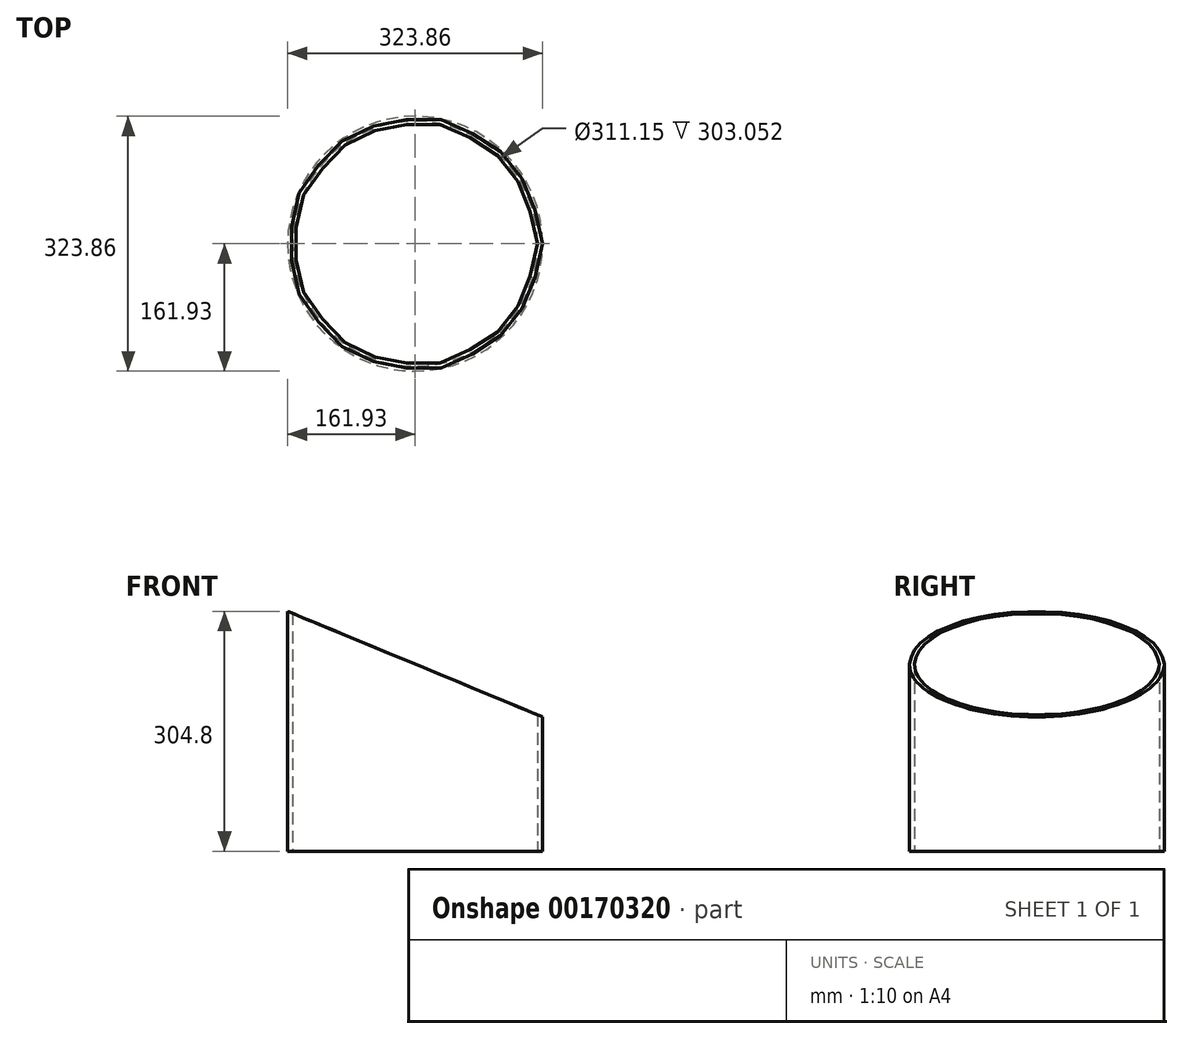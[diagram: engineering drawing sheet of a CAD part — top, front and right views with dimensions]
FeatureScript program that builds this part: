
annotation { "Feature Type Name" : "Feature", "Feature Type Description" : "" }
export const myFeature = defineFeature(function(context is Context, id is Id, definition is map)
    precondition{}
    {
        {
            var Q0;
            Q0=qCreatedBy(makeId("Top.planeOp"),FACE);
            var sketch = newSketch(context, id + "F0", { "sketchPlane" : qUnion([Q0])});
            skCircle(sketch, "E0", {"center": v(0, 0) * mm, "radius": 161.93 * mm});
            skCircle(sketch, "E1.0", {"center": v(0, 0) * mm, "radius": 155.58 * mm});
            skSolve(sketch);
        }
        {
            var Q0;
            Q0=makeQuery(id+"F0.imprint","IMPRINT",FACE,{"disambiguationData":[TD([[makeQuery(id+"F0.imprint","IMPRINT",EDGE,{"derivedFrom":sQuery(id+"F0.wireOp",EDGE,"E1.0")}),-1.0]])]});
            extrude(context, id + "F1", {"entities" : qUnion([Q0]), "depth" : 304.8 * mm});
        }
        {
            var Q0;
            Q0=qCreatedBy(makeId("Front.planeOp"),FACE);
            var sketch = newSketch(context, id + "F2", { "sketchPlane" : qUnion([Q0])});
            skLineSegment(sketch, "E2", {"start": v(0, 0) * mm, "end": v(0, 229.3) * mm, "construction": true});
            skLineSegment(sketch, "E3", {"start": v(0, 229.3) * mm, "end": v(-161.93, 229.3) * mm, "construction": true});
            skLineSegment(sketch, "E4", {"start": v(-161.93, 229.3) * mm, "end": v(-161.93, 304.8) * mm, "construction": true});
            skLineSegment(sketch, "E5", {"start": v(-161.93, 304.8) * mm, "end": v(161.93, 170.66) * mm});
            skLineSegment(sketch, "E6", {"start": v(-161.93, 304.8) * mm, "end": v(-161.93, 423.7) * mm});
            skLineSegment(sketch, "E7", {"start": v(-161.93, 423.7) * mm, "end": v(165.99, 433.47) * mm});
            skLineSegment(sketch, "E8", {"start": v(165.99, 433.47) * mm, "end": v(161.92, 170.66) * mm});
            skSolve(sketch);
        }
        {
            var Q0;
            Q0 = qSketchRegion(id + "F2", true);
            extrude(context, id + "F3", {"entities" : qUnion([Q0]), "operationType" : NewBodyOperationType.REMOVE, "endBound" : BoundingType.THROUGH_ALL, "oppositeDirection" : true, "depth" : 25.4 * mm, "hasSecondDirection" : true, "secondDirectionBound" : SecondDirectionBoundingType.THROUGH_ALL, "secondDirectionOppositeDirection" : false, "secondDirectionDepth" : 25.4 * mm});
        }
    });
